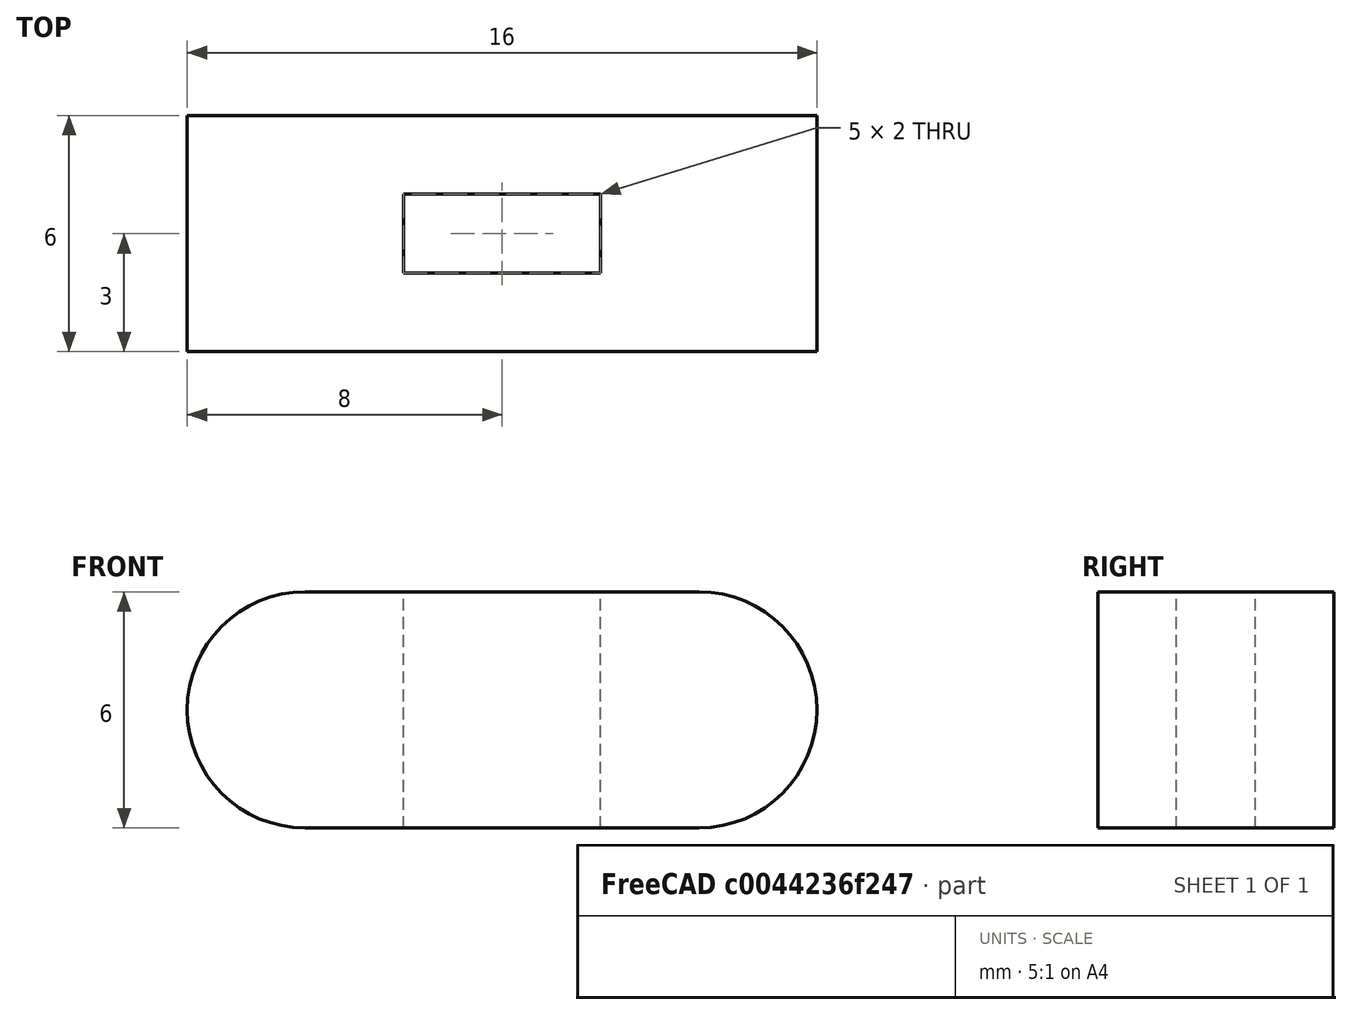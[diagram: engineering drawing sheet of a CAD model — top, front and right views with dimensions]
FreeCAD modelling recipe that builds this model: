
FCSTD DOCUMENT  (FreeCAD 0.20R29410 (Git))
Label: SlideLeft
License: All rights reserved
LicenseURL: http://en.wikipedia.org/wiki/All_rights_reserved
objects: Part::Cylinder×2, Part::Box×2, Spreadsheet::Sheet×1, Part::MultiFuse×1, Part::Cut×1
note: 6 computed .brp shape members not serialized (recipe doc carries the construction recipe); baked Part::Feature solids carry a one-line shape summary decoded from their .brp

FEATURE [Spreadsheet::Sheet] Spreadsheet  label="SS"
  cells = A2=InsertHeight; B2(InsertHeight)==6mm; A3=InsertLength; B3(InsertLength)==5mm; A4=InsertWidth; B4(InsertWidth)==2mm; A5=InsertCap; B5(InsertCap)==2mm; A7=SlideWidth; B7(SlideWidth)==6mm; A8=SlideLength; B8(SlideLength)==10mm
FEATURE [Part::Cylinder] Cylinder  label="SlideLeftSide"
  Angle = 360
  AttacherType = Attacher::AttachEngine3D
  FirstAngle = 0
  Height = 6
  Placement = pos=(-5,3,0) rot=(1,0,0;1.5708rad)
  Radius = 3
  SecondAngle = 0
  expr: .Placement.Base.x = -<<SS>>.SlideLength / 2
  expr: .Placement.Base.y = <<SS>>.SlideWidth / 2
  expr: Height = <<SS>>.SlideWidth
  expr: Radius = <<SS>>.SlideWidth / 2
FEATURE [Part::Cylinder] Cylinder001  label="SlideRightSide"
  Angle = 360
  AttacherType = Attacher::AttachEngine3D
  FirstAngle = 0
  Height = 6
  Placement = pos=(5,3,0) rot=(1,0,0;1.5708rad)
  Radius = 3
  SecondAngle = 0
  expr: .Placement.Base.x = <<SS>>.SlideLength / 2
  expr: .Placement.Base.y = <<SS>>.SlideWidth / 2
  expr: Height = <<SS>>.SlideWidth
  expr: Radius = <<SS>>.SlideWidth / 2
FEATURE [Part::Box] Box  label="SlideBox"
  AttacherType = Attacher::AttachEngine3D
  Height = 6
  Length = 10
  Placement = pos=(-5,-3,-3) rot=(0,0,1;0rad)
  Width = 6
  expr: .Placement.Base.x = -<<SS>>.SlideLength / 2
  expr: .Placement.Base.y = -<<SS>>.SlideWidth / 2
  expr: .Placement.Base.z = -<<SS>>.SlideWidth / 2
  expr: Height = <<SS>>.SlideWidth
  expr: Length = <<SS>>.SlideLength
  expr: Width = <<SS>>.SlideWidth
FEATURE [Part::MultiFuse] Fusion  label="SlideBody"
  Placement = pos=(0,0,3) rot=(0,0,1;0rad)
  Shapes = -> [Cylinder,Cylinder001,Box]
  expr: .Placement.Base.z = <<SS>>.SlideWidth / 2
FEATURE [Part::Box] Box001  label="Insert"
  AttacherType = Attacher::AttachEngine3D
  Height = 6
  Length = 5
  Placement = pos=(-2.5,-1,0) rot=(0,0,1;0rad)
  Width = 2
  expr: .Placement.Base.x = -<<SS>>.InsertLength / 2
  expr: .Placement.Base.y = -<<SS>>.InsertWidth / 2
  expr: Height = <<SS>>.InsertHeight
  expr: Length = <<SS>>.InsertLength
  expr: Width = <<SS>>.InsertWidth
FEATURE [Part::Cut] Cut  label="SlideTotal"
  Base = -> Fusion
  Tool = -> Box001
